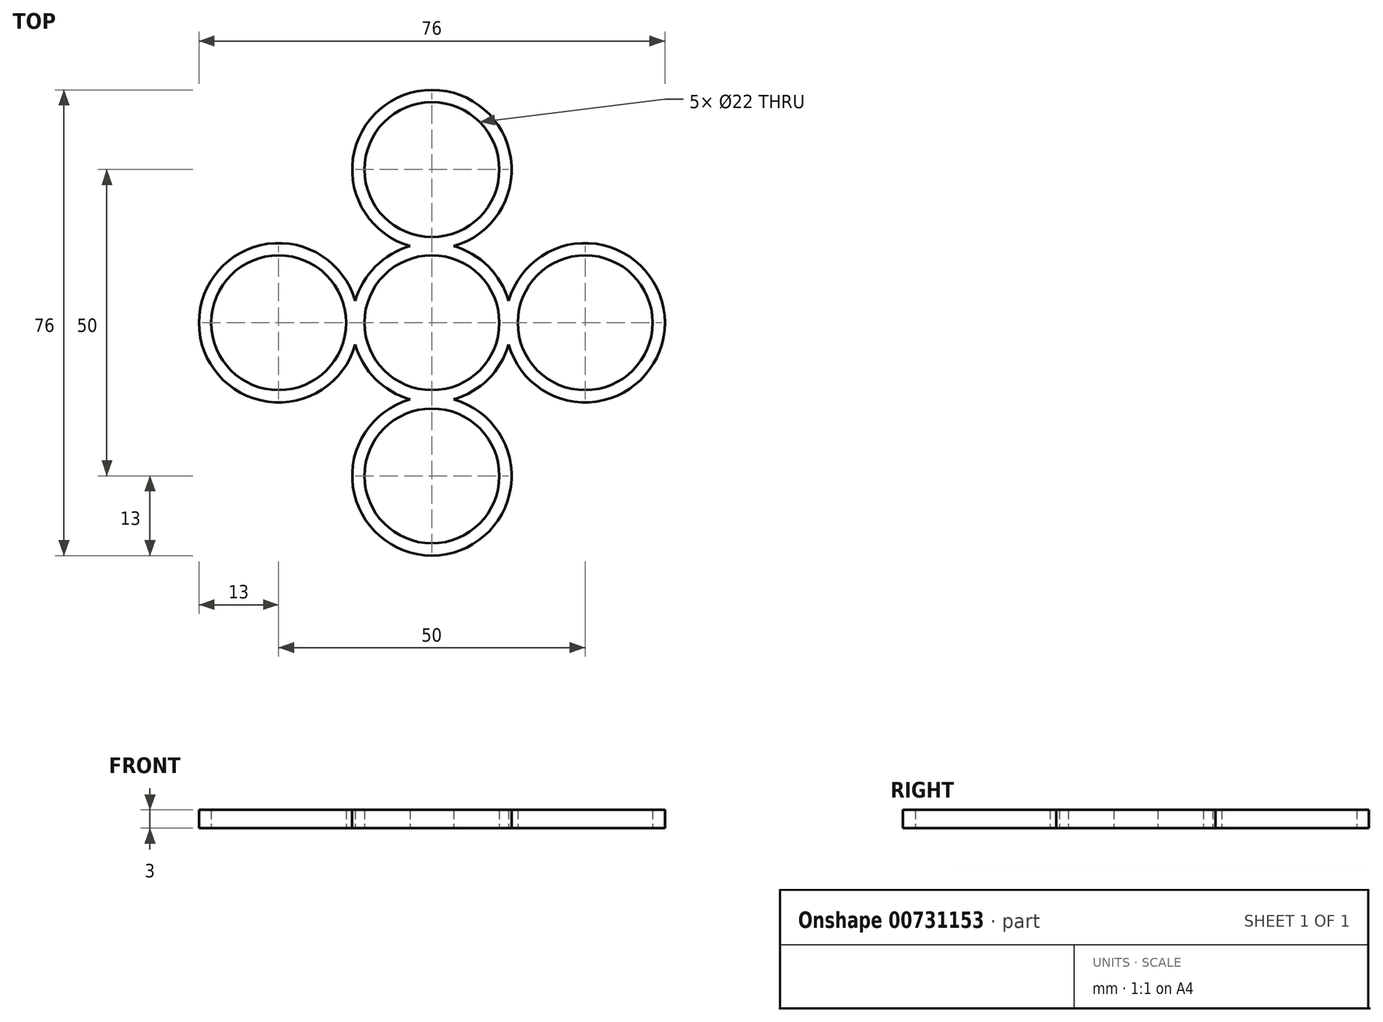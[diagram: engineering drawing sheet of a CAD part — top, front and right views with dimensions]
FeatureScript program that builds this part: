
annotation { "Feature Type Name" : "Feature", "Feature Type Description" : "" }
export const myFeature = defineFeature(function(context is Context, id is Id, definition is map)
    precondition{}
    {
        {
            var Q0;
            Q0=qCreatedBy(makeId("Top.planeOp"),FACE);
            var sketch = newSketch(context, id + "F0", { "sketchPlane" : qUnion([Q0])});
            skArc(sketch, "E0", {"start": v(0, 11) * mm, "mid": v(-7.78, 7.78) * mm, "end": v(-11, 0) * mm});
            skArc(sketch, "E1", {"start": v(-3.57, 12.5) * mm, "mid": v(-9.2, 9.2) * mm, "end": v(-12.5, 3.57) * mm});
            skLineSegment(sketch, "E2", {"start": v(0, 0) * mm, "end": v(0, 25) * mm});
            skCircle(sketch, "E3", {"center": v(0, 25) * mm, "radius": 11 * mm});
            skArc(sketch, "E4", {"start": v(3.57, 12.5) * mm, "mid": v(0, 38) * mm, "end": v(-3.57, 12.5) * mm});
            skLineSegment(sketch, "E5", {"start": v(-13, 0) * mm, "end": v(-11, 0) * mm});
            skArc(sketch, "E6.trimOffspring", {"start": v(12.5, 3.57) * mm, "mid": v(9.2, 9.2) * mm, "end": v(3.57, 12.5) * mm});
            skPoint(sketch, "E7.orphan", {"position": v(-28.16, 0) * mm});
            skLineSegment(sketch, "E8.trimOffspring", {"start": v(11, 0) * mm, "end": v(13, 0) * mm});
            skCircle(sketch, "E9.1.0", {"center": v(-25, 0) * mm, "radius": 11 * mm});
            skArc(sketch, "E9.1.1", {"start": v(-12.5, 3.57) * mm, "mid": v(-38, 0) * mm, "end": v(-12.5, -3.57) * mm});
            skCircle(sketch, "E9.2.0", {"center": v(0, -25) * mm, "radius": 11 * mm});
            skArc(sketch, "E9.2.1", {"start": v(-3.57, -12.5) * mm, "mid": v(0, -38) * mm, "end": v(3.57, -12.5) * mm});
            skArc(sketch, "E9.2.2", {"start": v(-12.5, -3.57) * mm, "mid": v(-9.2, -9.2) * mm, "end": v(-3.57, -12.5) * mm});
            skArc(sketch, "E9.2.3", {"start": v(-11, 0) * mm, "mid": v(0, -11) * mm, "end": v(11, 0) * mm});
            skArc(sketch, "E9.2.4", {"start": v(3.57, -12.5) * mm, "mid": v(9.2, -9.2) * mm, "end": v(12.5, -3.57) * mm});
            skCircle(sketch, "E9.3.0", {"center": v(25, 0) * mm, "radius": 11 * mm});
            skArc(sketch, "E9.3.1", {"start": v(12.5, -3.57) * mm, "mid": v(38, 0) * mm, "end": v(12.5, 3.57) * mm});
            skArc(sketch, "E9.3.3", {"start": v(11, 0) * mm, "mid": v(7.78, 7.78) * mm, "end": v(0, 11) * mm});
            skPoint(sketch, "E10.orphan", {"position": v(0, -13) * mm});
            skPoint(sketch, "E11.orphan", {"position": v(0, 13) * mm});
            skPoint(sketch, "E12.orphan", {"position": v(-13, 0) * mm});
            skPoint(sketch, "E13.orphan", {"position": v(0, -11) * mm});
            skPoint(sketch, "E14.orphan", {"position": v(13, 0) * mm});
            skSolve(sketch);
        }
        {
            var Q0;
            Q0 = qSketchRegion(id + "F0", true);
            extrude(context, id + "F1", {"entities" : qUnion([Q0]), "depth" : 3 * mm, "offsetDistance" : 25 * mm});
        }
    });
